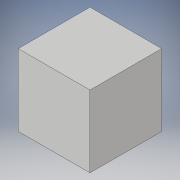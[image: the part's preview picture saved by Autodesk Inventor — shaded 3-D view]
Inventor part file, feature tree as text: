
AUTODESK INVENTOR PART (.ipt)
format: ipt  version: 2017 (Build 210142000, 142)  size: 82,944 bytes
history: native  units: in
note: dims shown in document units (in); Inventor stores cm internally (conversion verified against a paired STEP export)
features: extrude x1, sketch x1
ambient origin geometry x8: Origin, YZ Plane, XZ Plane, XY Plane, X Axis, Y Axis, Z Axis, Center Point
bodies: Solid1 (feature_tree)
feature tree (2):
  extrude  "Extrusion1"  Depth=0.5in
  sketch  "Sketch1"  dims[d0=0.5in d1=0.5in d2=0.5in d3=0.0in]
